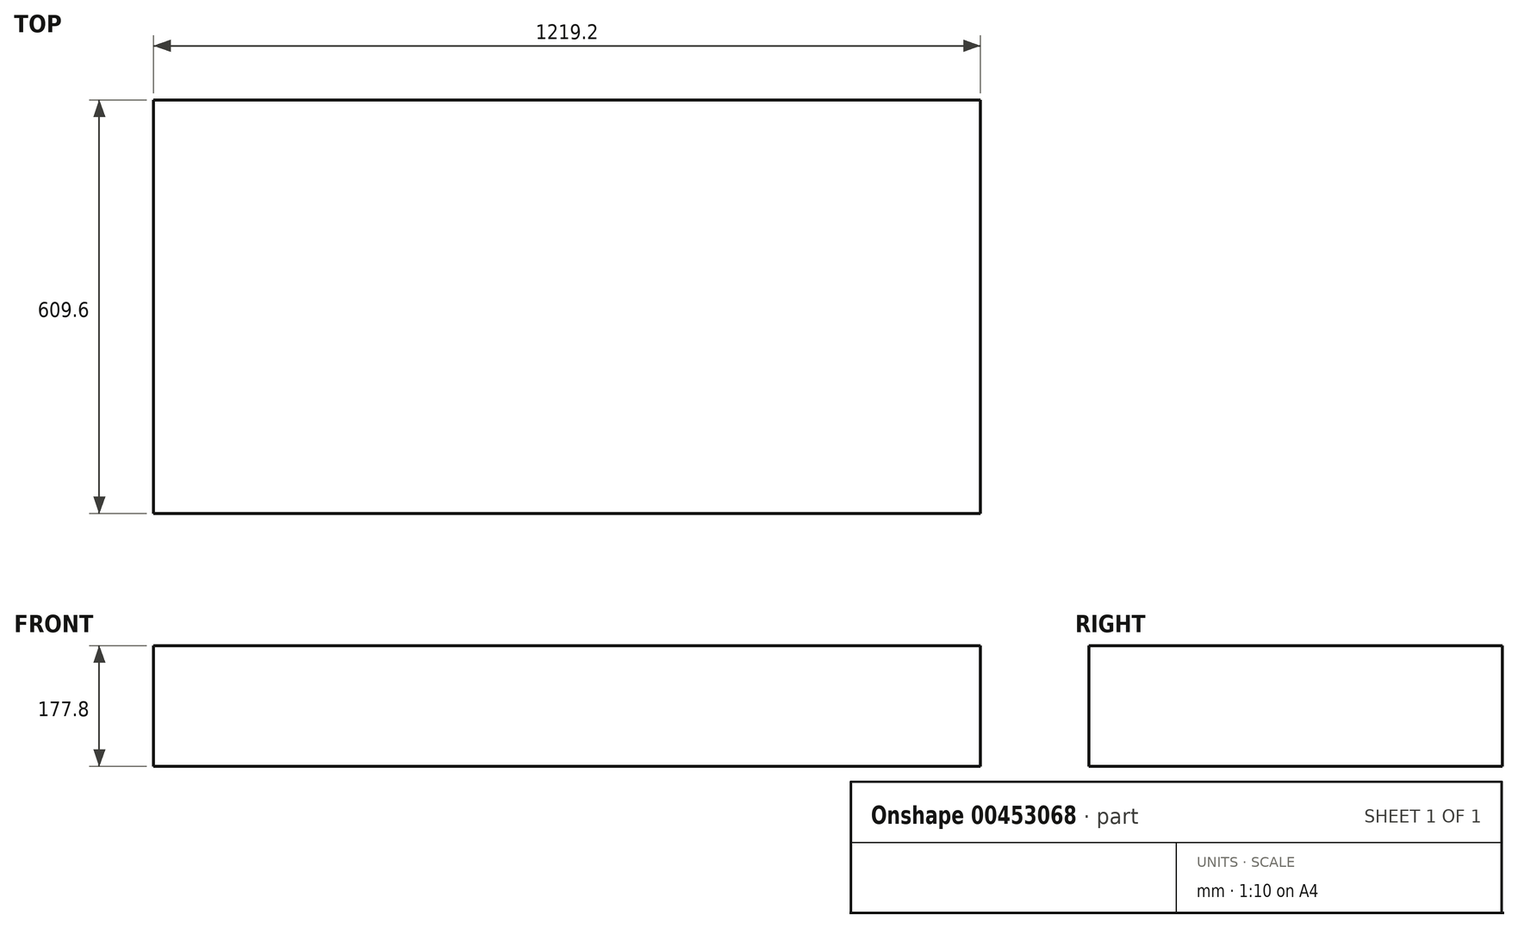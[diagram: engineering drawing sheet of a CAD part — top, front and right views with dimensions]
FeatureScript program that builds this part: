
annotation { "Feature Type Name" : "Feature", "Feature Type Description" : "" }
export const myFeature = defineFeature(function(context is Context, id is Id, definition is map)
    precondition{}
    {
        {
            var Q0;
            Q0=qCreatedBy(makeId("Top.planeOp"),FACE);
            var sketch = newSketch(context, id + "F0", { "sketchPlane" : qUnion([Q0])});
            skLineSegment(sketch, "E0.bottom", {"start": v(609.6, 304.8) * mm, "end": v(-609.6, 304.8) * mm});
            skLineSegment(sketch, "E0.top", {"start": v(609.6, -304.8) * mm, "end": v(-609.6, -304.8) * mm});
            skLineSegment(sketch, "E0.left", {"start": v(609.6, 304.8) * mm, "end": v(609.6, -304.8) * mm});
            skLineSegment(sketch, "E0.right", {"start": v(-609.6, 304.8) * mm, "end": v(-609.6, -304.8) * mm});
            skPoint(sketch, "E0.middle", {"position": v(0, 0) * mm});
            skSolve(sketch);
        }
        {
            var Q0;
            Q0 = qSketchRegion(id + "F0", true);
            extrude(context, id + "F1", {"entities" : qUnion([Q0]), "depth" : 177.8 * mm, "offsetDistance" : 25.4 * mm});
        }
    });
